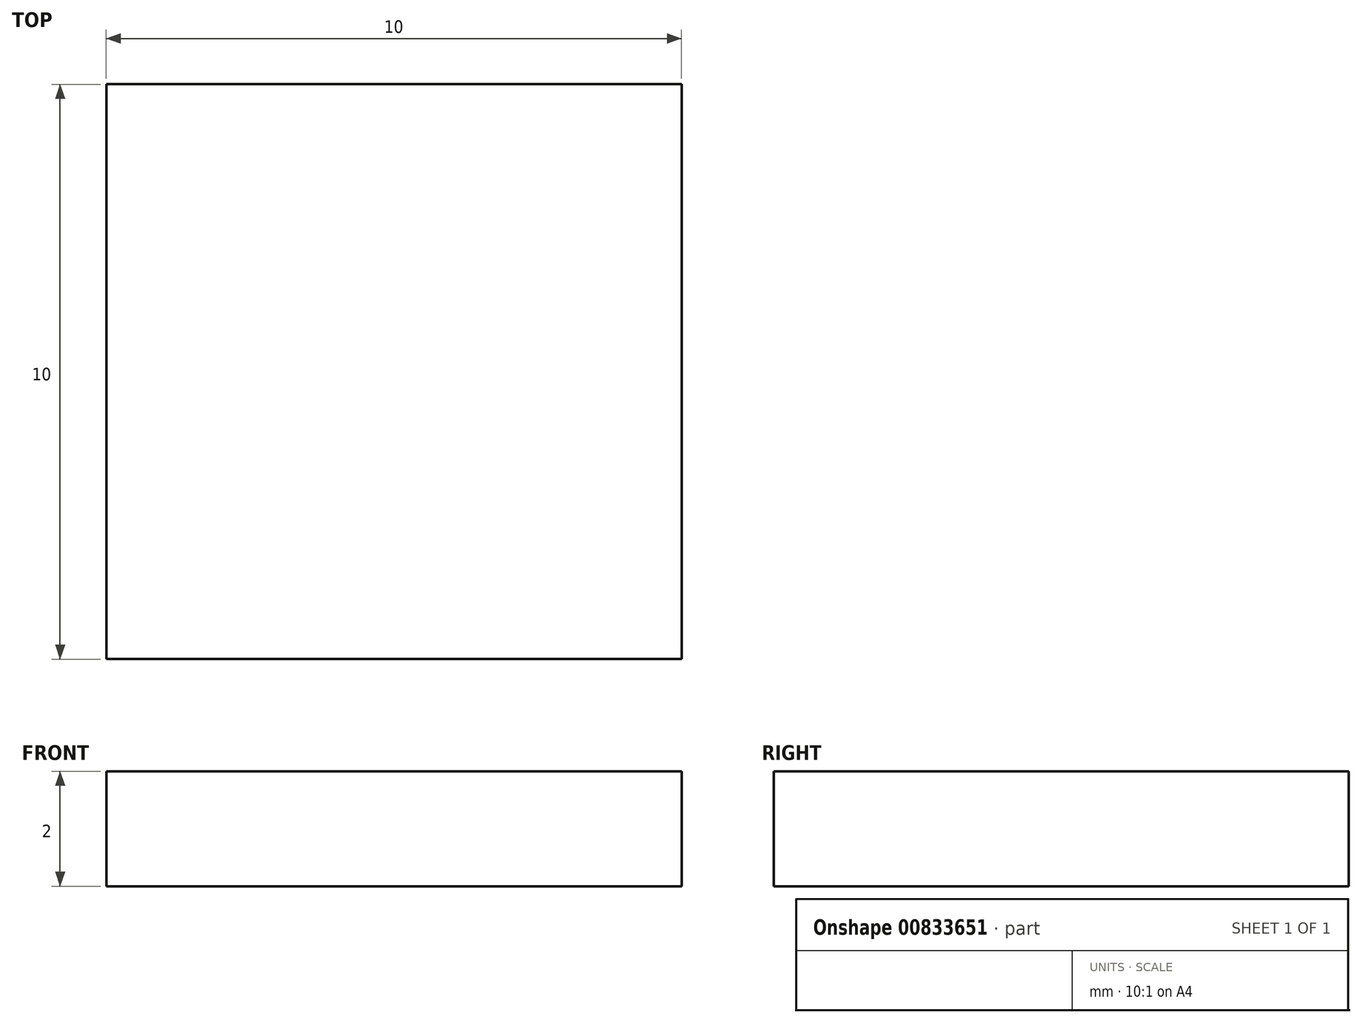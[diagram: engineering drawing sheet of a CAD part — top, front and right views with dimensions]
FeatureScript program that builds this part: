
annotation { "Feature Type Name" : "Feature", "Feature Type Description" : "" }
export const myFeature = defineFeature(function(context is Context, id is Id, definition is map)
    precondition{}
    {
        {
            var Q0;
            Q0=qCreatedBy(makeId("Top.planeOp"),FACE);
            var sketch = newSketch(context, id + "F0", { "sketchPlane" : qUnion([Q0])});
            skLineSegment(sketch, "E0.bottom", {"start": v(-9.25, 25.4) * mm, "end": v(-19.25, 25.4) * mm});
            skLineSegment(sketch, "E0.left", {"start": v(-9.25, 25.4) * mm, "end": v(-9.25, 15.4) * mm});
            skLineSegment(sketch, "E1", {"start": v(-14.25, 21.65) * mm, "end": v(-14.25, 19.15) * mm});
            skLineSegment(sketch, "E2", {"start": v(-19.25, 19.15) * mm, "end": v(-19.25, 15.4) * mm});
            skLineSegment(sketch, "E3", {"start": v(-19.25, 21.65) * mm, "end": v(-19.25, 25.4) * mm});
            skLineSegment(sketch, "E4", {"start": v(-19.25, 15.4) * mm, "end": v(-9.25, 15.4) * mm});
            skLineSegment(sketch, "E5", {"start": v(-19.25, 19.15) * mm, "end": v(-19.25, 21.65) * mm});
            skSolve(sketch);
        }
        {
            var Q0;
            Q0=makeQuery(id+"F0.imprint","IMPRINT",FACE,{"disambiguationData":[TD([[makeQuery(id+"F0.imprint","IMPRINT",EDGE,{"derivedFrom":sQuery(id+"F0.wireOp",EDGE,"E0.bottom")}),1.0]])]});
            extrude(context, id + "F1", {"entities" : qUnion([Q0]), "depth" : 2 * mm, "offsetDistance" : 25 * mm});
        }
    });
